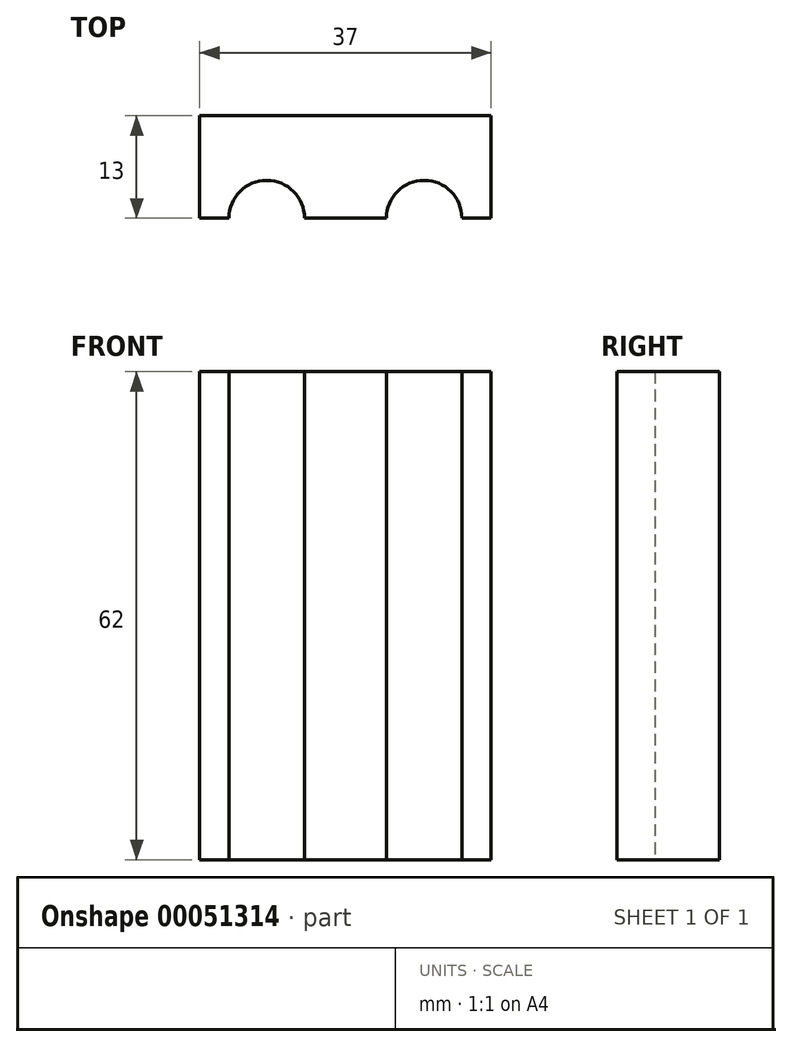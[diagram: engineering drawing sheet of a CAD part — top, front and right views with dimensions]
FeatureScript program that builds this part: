
annotation { "Feature Type Name" : "Feature", "Feature Type Description" : "" }
export const myFeature = defineFeature(function(context is Context, id is Id, definition is map)
    precondition{}
    {
        {
            var Q0;
            Q0=qCreatedBy(makeId("Top.planeOp"),FACE);
            var sketch = newSketch(context, id + "F0", { "sketchPlane" : qUnion([Q0])});
            skLineSegment(sketch, "E0.bottom", {"start": v(0, 0) * mm, "end": v(37, 0) * mm});
            skLineSegment(sketch, "E0.top", {"start": v(0, 15) * mm, "end": v(37, 15) * mm});
            skLineSegment(sketch, "E0.left", {"start": v(0, 0) * mm, "end": v(0, 15) * mm});
            skLineSegment(sketch, "E0.right", {"start": v(37, 0) * mm, "end": v(37, 15) * mm});
            skSolve(sketch);
        }
        {
            var Q0;
            Q0=makeQuery(id+"F0.imprint","IMPRINT",FACE,{"disambiguationData":[TD([[makeQuery(id+"F0.imprint","IMPRINT",EDGE,{"derivedFrom":sQuery(id+"F0.wireOp",EDGE,"E0.bottom")}),1.0]])]});
            extrude(context, id + "F1", {"entities" : qUnion([Q0]), "depth" : 62 * mm});
        }
        {
            var Q0;
            Q0=makeQuery(id+"F1.opExtrude","CAP_FACE",FACE,{"disambiguationData":[OSD([sQuery(id+"F0.wireOp",EDGE,"E0.bottom"),sQuery(id+"F0.wireOp",EDGE,"E0.top"),sQuery(id+"F0.wireOp",EDGE,"E0.left"),sQuery(id+"F0.wireOp",EDGE,"E0.right")])],"isStart":true});
            var sketch = newSketch(context, id + "F2", { "sketchPlane" : qUnion([Q0])});
            skLineSegment(sketch, "E1", {"start": v(18.5, 0) * mm, "end": v(18.5, -15) * mm, "construction": true});
            skLineSegment(sketch, "E2", {"start": v(8.5, 0) * mm, "end": v(8.5, -15) * mm, "construction": true});
            skLineSegment(sketch, "E3", {"start": v(28.5, 0) * mm, "end": v(28.5, -15) * mm, "construction": true});
            skArc(sketch, "E4", {"start": v(3.7, 0) * mm, "mid": v(8.5, -4.8) * mm, "end": v(13.3, 0) * mm});
            skArc(sketch, "E5", {"start": v(23.7, 0) * mm, "mid": v(28.5, -4.8) * mm, "end": v(33.3, 0) * mm});
            skSolve(sketch);
        }
        {
            var Q0;
            {var subQ0=sQuery(id+"F2.wireOp",EDGE,"E4");Q0=makeQuery(id+"F2.imprint","IMPRINT",FACE,{"disambiguationData":[TD([[makeQuery(id+"F2.imprint","IMPRINT",EDGE,{"derivedFrom":subQ0}),1.0]])]});}
            var Q1;
            {var subQ0=sQuery(id+"F2.wireOp",EDGE,"E5");Q1=makeQuery(id+"F2.imprint","IMPRINT",FACE,{"disambiguationData":[TD([[makeQuery(id+"F2.imprint","IMPRINT",EDGE,{"derivedFrom":subQ0}),1.0]])]});}
            extrude(context, id + "F3", {"entities" : qUnion([Q0, Q1]), "operationType" : NewBodyOperationType.REMOVE, "endBound" : BoundingType.THROUGH_ALL, "oppositeDirection" : true, "depth" : 25 * mm});
        }
        {
            var Q0;
            Q0=makeQuery(id+"F1.opExtrude","SWEPT_FACE",FACE,{"disambiguationData":[OSD([sQuery(id+"F0.wireOp",EDGE,"E0.top")])]});
            extrude(context, id + "F4", {"entities" : qUnion([Q0]), "operationType" : NewBodyOperationType.REMOVE, "oppositeDirection" : true, "depth" : 2 * mm, "offsetDistance" : 25 * mm});
        }
    });
